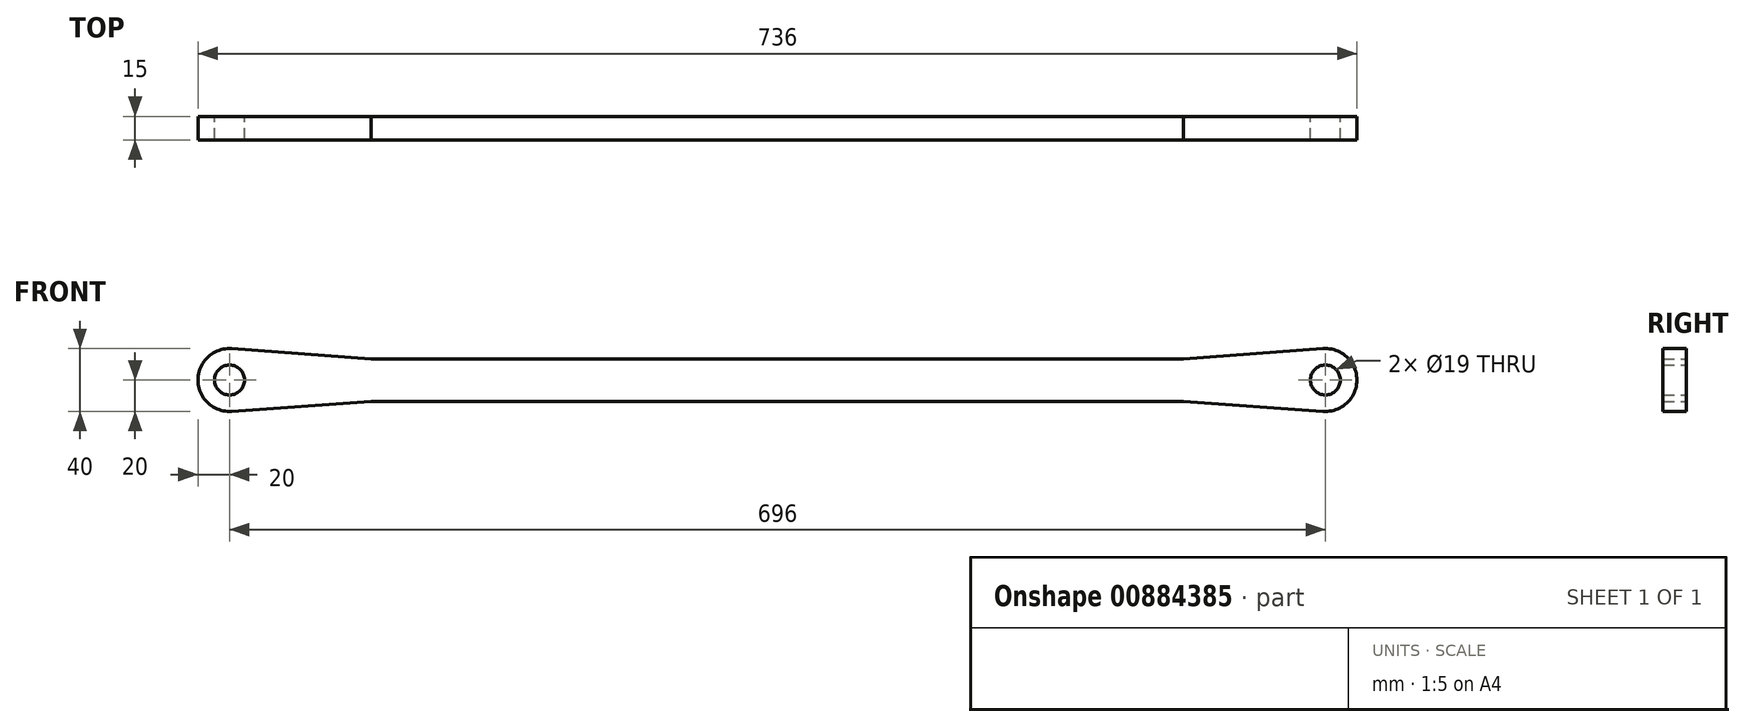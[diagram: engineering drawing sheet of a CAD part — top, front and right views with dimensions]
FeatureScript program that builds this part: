
annotation { "Feature Type Name" : "Feature", "Feature Type Description" : "" }
export const myFeature = defineFeature(function(context is Context, id is Id, definition is map)
    precondition{}
    {
        {
            var Q0;
            Q0=qCreatedBy(makeId("Front.planeOp"),FACE);
            var sketch = newSketch(context, id + "F0", { "sketchPlane" : qUnion([Q0])});
            skLineSegment(sketch, "E0.bottom", {"start": v(348, 13.5) * mm, "end": v(-348, 13.5) * mm});
            skLineSegment(sketch, "E0.top", {"start": v(348, -13.5) * mm, "end": v(-348, -13.5) * mm});
            skLineSegment(sketch, "E0.left", {"start": v(348, 13.5) * mm, "end": v(348, -13.5) * mm});
            skLineSegment(sketch, "E0.right", {"start": v(-348, 13.5) * mm, "end": v(-348, -13.5) * mm});
            skPoint(sketch, "E0.middle", {"position": v(0, 0) * mm});
            skLineSegment(sketch, "E1", {"start": v(-348, 0) * mm, "end": v(348, 0) * mm, "construction": true});
            skCircle(sketch, "E2", {"center": v(-348, 0) * mm, "radius": 20 * mm});
            skCircle(sketch, "E3", {"center": v(-348, 0) * mm, "radius": 9.5 * mm});
            skLineSegment(sketch, "E4", {"start": v(-258, 13.5) * mm, "end": v(-346.55, 19.95) * mm});
            skLineSegment(sketch, "E5", {"start": v(-258, -13.5) * mm, "end": v(-346.55, -19.95) * mm});
            skCircle(sketch, "E6", {"center": v(348, 0) * mm, "radius": 20 * mm});
            skCircle(sketch, "E7", {"center": v(348, 0) * mm, "radius": 9.5 * mm});
            skLineSegment(sketch, "E8", {"start": v(258, 13.5) * mm, "end": v(346.55, 19.95) * mm});
            skLineSegment(sketch, "E9", {"start": v(258, -13.5) * mm, "end": v(346.55, -19.95) * mm});
            skSolve(sketch);
        }
        {
            var Q0;
            {var subQ0=sQuery(id+"F0.wireOp",EDGE,"E0.right");var subQ5=sQuery(id+"F0.wireOp",EDGE,"E0.bottom");var subQ6=makeQuery(id+"F0.imprint","INTERSECT",VERTEX,{"derivedFrom":[subQ5,subQ0]});Q0=makeQuery(id+"F0.imprint","IMPRINT",FACE,{"disambiguationData":[TD([[makeQuery(id+"F0.imprint","IMPRINT",EDGE,{"disambiguationData":[TD([[subQ6,1.0]])],"derivedFrom":subQ5}),-1.0]])]});}
            var Q1;
            {var subQ0=sQuery(id+"F0.wireOp",EDGE,"E4");Q1=makeQuery(id+"F0.imprint","IMPRINT",FACE,{"disambiguationData":[TD([[makeQuery(id+"F0.imprint","IMPRINT",EDGE,{"derivedFrom":subQ0}),1.0]])]});}
            var Q2;
            {var subQ0=sQuery(id+"F0.wireOp",EDGE,"E5");Q2=makeQuery(id+"F0.imprint","IMPRINT",FACE,{"disambiguationData":[TD([[makeQuery(id+"F0.imprint","IMPRINT",EDGE,{"derivedFrom":subQ0}),-1.0]])]});}
            var Q3;
            {var subQ0=sQuery(id+"F0.wireOp",EDGE,"E0.right");var subQ5=sQuery(id+"F0.wireOp",EDGE,"E0.bottom");var subQ6=makeQuery(id+"F0.imprint","INTERSECT",VERTEX,{"derivedFrom":[subQ5,subQ0]});Q3=makeQuery(id+"F0.imprint","IMPRINT",FACE,{"disambiguationData":[TD([[makeQuery(id+"F0.imprint","IMPRINT",EDGE,{"disambiguationData":[TD([[subQ6,1.0]])],"derivedFrom":subQ5}),1.0]])]});}
            var Q4;
            {var subQ0=sQuery(id+"F0.wireOp",EDGE,"E0.bottom");var subQ8=makeQuery(id+"F0.imprint","INTERSECT",VERTEX,{"derivedFrom":[subQ0,sQuery(id+"F0.wireOp",EDGE,"E8")]});Q4=makeQuery(id+"F0.imprint","IMPRINT",FACE,{"disambiguationData":[TD([[makeQuery(id+"F0.imprint","IMPRINT",EDGE,{"disambiguationData":[TD([[subQ8,1.0]])],"derivedFrom":subQ0}),1.0]])]});}
            var Q5;
            {var subQ0=sQuery(id+"F0.wireOp",EDGE,"E8");Q5=makeQuery(id+"F0.imprint","IMPRINT",FACE,{"disambiguationData":[TD([[makeQuery(id+"F0.imprint","IMPRINT",EDGE,{"derivedFrom":subQ0}),-1.0]])]});}
            var Q6;
            {var subQ0=sQuery(id+"F0.wireOp",EDGE,"E9");Q6=makeQuery(id+"F0.imprint","IMPRINT",FACE,{"disambiguationData":[TD([[makeQuery(id+"F0.imprint","IMPRINT",EDGE,{"derivedFrom":subQ0}),1.0]])]});}
            var Q7;
            {var subQ0=sQuery(id+"F0.wireOp",EDGE,"E0.left");var subQ5=sQuery(id+"F0.wireOp",EDGE,"E0.bottom");var subQ6=makeQuery(id+"F0.imprint","INTERSECT",VERTEX,{"derivedFrom":[subQ5,subQ0]});Q7=makeQuery(id+"F0.imprint","IMPRINT",FACE,{"disambiguationData":[TD([[makeQuery(id+"F0.imprint","IMPRINT",EDGE,{"disambiguationData":[TD([[subQ6,-1.0]])],"derivedFrom":subQ5}),1.0]])]});}
            var Q8;
            {var subQ0=sQuery(id+"F0.wireOp",EDGE,"E0.left");var subQ5=sQuery(id+"F0.wireOp",EDGE,"E0.bottom");var subQ6=makeQuery(id+"F0.imprint","INTERSECT",VERTEX,{"derivedFrom":[subQ5,subQ0]});Q8=makeQuery(id+"F0.imprint","IMPRINT",FACE,{"disambiguationData":[TD([[makeQuery(id+"F0.imprint","IMPRINT",EDGE,{"disambiguationData":[TD([[subQ6,-1.0]])],"derivedFrom":subQ5}),-1.0]])]});}
            extrude(context, id + "F1", {"entities" : qUnion([Q0, Q1, Q2, Q3, Q4, Q5, Q6, Q7, Q8]), "endBound" : BoundingType.SYMMETRIC, "depth" : 15 * mm, "offsetDistance" : 25 * mm});
        }
    });
